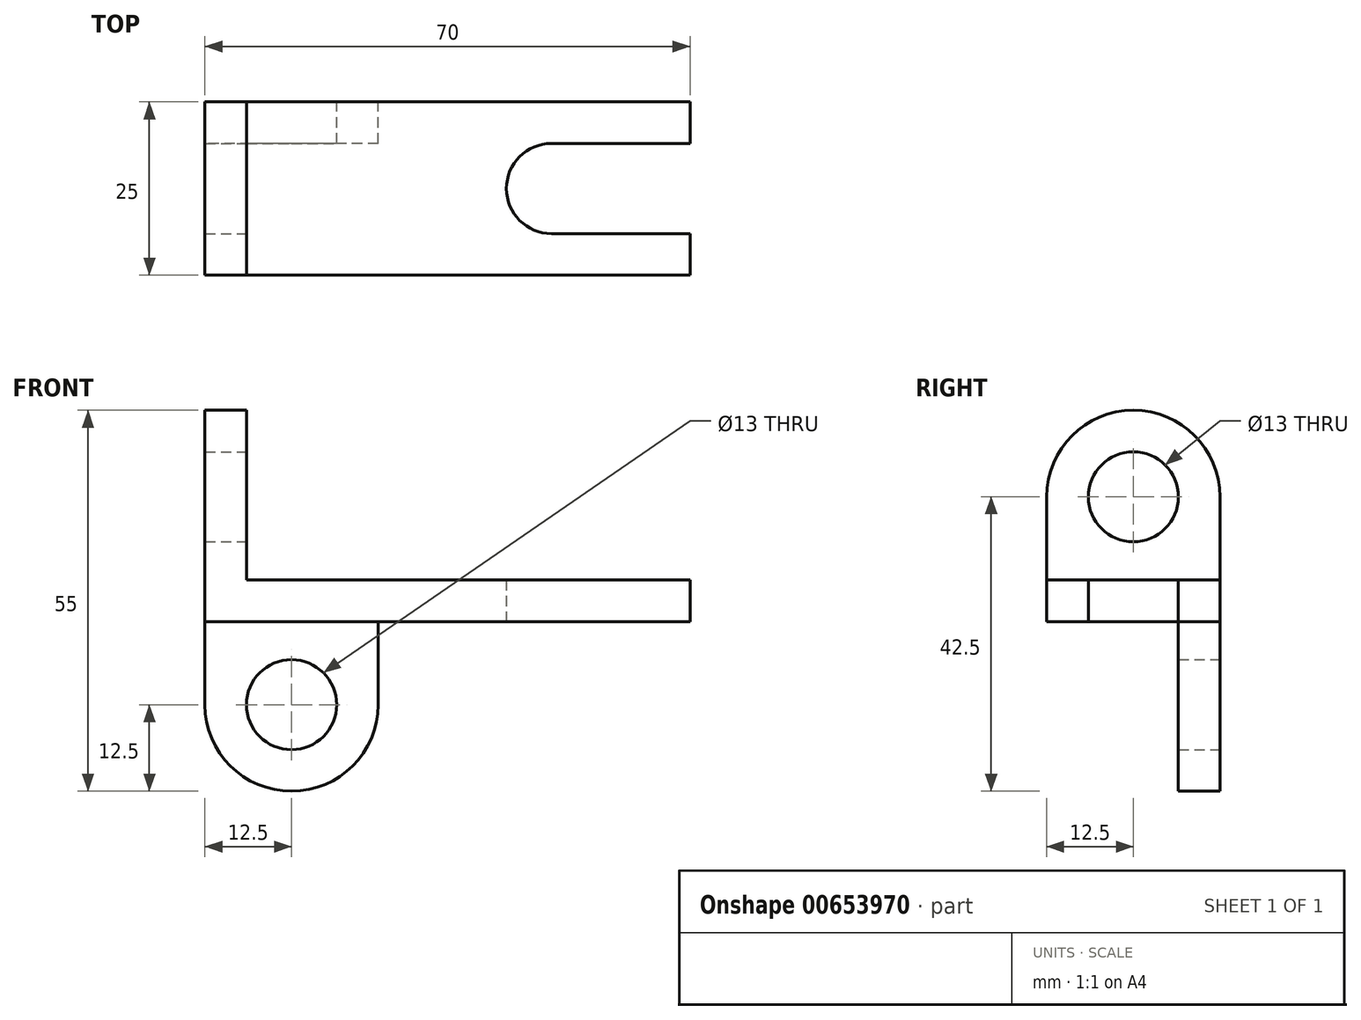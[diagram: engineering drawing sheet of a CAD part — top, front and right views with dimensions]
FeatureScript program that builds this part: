
annotation { "Feature Type Name" : "Feature", "Feature Type Description" : "" }
export const myFeature = defineFeature(function(context is Context, id is Id, definition is map)
    precondition{}
    {
        {
            var Q0;
            Q0=qCreatedBy(makeId("Top.planeOp"),FACE);
            var sketch = newSketch(context, id + "F0", { "sketchPlane" : qUnion([Q0])});
            skLineSegment(sketch, "E0.bottom", {"start": v(32, -12.5) * mm, "end": v(-32, -12.5) * mm});
            skLineSegment(sketch, "E0.top", {"start": v(32, 12.5) * mm, "end": v(-32, 12.5) * mm});
            skLineSegment(sketch, "E0.left", {"start": v(32, -12.5) * mm, "end": v(32, 12.5) * mm});
            skLineSegment(sketch, "E0.right", {"start": v(-32, -12.5) * mm, "end": v(-32, 12.5) * mm});
            skPoint(sketch, "E0.middle", {"position": v(0, 0) * mm});
            skLineSegment(sketch, "E1.bottom", {"start": v(32, 6.5) * mm, "end": v(12, 6.5) * mm});
            skLineSegment(sketch, "E1.top", {"start": v(32, -6.5) * mm, "end": v(12, -6.5) * mm});
            skLineSegment(sketch, "E1.left", {"start": v(32, 6.5) * mm, "end": v(32, -6.5) * mm});
            skLineSegment(sketch, "E1.right", {"start": v(12, 6.5) * mm, "end": v(12, -6.5) * mm});
            skPoint(sketch, "E1.middle", {"position": v(22, 0) * mm});
            skCircle(sketch, "E2", {"center": v(12, 0) * mm, "radius": 6.5 * mm});
            skSolve(sketch);
        }
        {
            var Q0;
            {var subQ4=sQuery(id+"F0.wireOp",EDGE,"E0.bottom");Q0=makeQuery(id+"F0.imprint","IMPRINT",FACE,{"disambiguationData":[TD([[makeQuery(id+"F0.imprint","IMPRINT",EDGE,{"derivedFrom":subQ4}),-1.0]])]});}
            extrude(context, id + "F1", {"entities" : qUnion([Q0]), "depth" : 6 * mm, "offsetDistance" : 25 * mm});
        }
        {
            var Q0;
            Q0=makeQuery(id+"F1.opExtrude","SWEPT_FACE",FACE,{"disambiguationData":[OSD([sQuery(id+"F0.wireOp",EDGE,"E0.right")])]});
            var sketch = newSketch(context, id + "F2", { "sketchPlane" : qUnion([Q0])});
            skLineSegment(sketch, "E3.bottom", {"start": v(-12.5, 0) * mm, "end": v(12.5, 0) * mm});
            skLineSegment(sketch, "E3.top", {"start": v(-12.5, 18) * mm, "end": v(-6.5, 18) * mm});
            skLineSegment(sketch, "E3.left", {"start": v(-12.5, 0) * mm, "end": v(-12.5, 18) * mm});
            skLineSegment(sketch, "E3.right", {"start": v(12.5, 0) * mm, "end": v(12.5, 18) * mm});
            skArc(sketch, "E4", {"start": v(12.5, 18) * mm, "mid": v(0, 30.5) * mm, "end": v(-12.5, 18) * mm});
            skCircle(sketch, "E5", {"center": v(0, 18) * mm, "radius": 6.5 * mm});
            skLineSegment(sketch, "E6.trimOffspring", {"start": v(6.5, 18) * mm, "end": v(12.5, 18) * mm});
            skSolve(sketch);
        }
        {
            var Q0;
            {var subQ1=sQuery(id+"F0.wireOp",EDGE,"E0.right");var subQ5=makeQuery(id+"F1.opExtrude","CAP_EDGE",EDGE,{"disambiguationData":[OSD([subQ1])],"isStart":false});Q0=makeQuery(id+"F2.imprint","IMPRINT",FACE,{"disambiguationData":[TD([[makeQuery(id+"F2.imprint","IMPRINT",EDGE,{"derivedFrom":subQ5}),1.0]])]});}
            var Q1;
            {var subQ3=sQuery(id+"F2.wireOp",EDGE,"E4");Q1=makeQuery(id+"F2.imprint","IMPRINT",FACE,{"disambiguationData":[TD([[makeQuery(id+"F2.imprint","IMPRINT",EDGE,{"derivedFrom":subQ3}),1.0]])]});}
            var Q2;
            {var subQ11=sQuery(id+"F2.wireOp",EDGE,"E3.right");Q2=makeQuery(id+"F2.imprint","IMPRINT",FACE,{"disambiguationData":[TD([[makeQuery(id+"F2.imprint","IMPRINT",EDGE,{"derivedFrom":subQ11}),1.0]])]});}
            extrude(context, id + "F3", {"entities" : qUnion([Q0, Q1, Q2]), "operationType" : NewBodyOperationType.ADD, "depth" : 6 * mm, "offsetDistance" : 25 * mm});
        }
        {
            var Q0;
            Q0=makeQuery(id+"F3.boolean.opBoolean","MERGE",FACE,{"derivedFrom":[makeQuery(id+"F1.opExtrude","SWEPT_FACE",FACE,{"disambiguationData":[OSD([sQuery(id+"F0.wireOp",EDGE,"E0.top")])]}),makeQuery(id+"F3.opExtrude","SWEPT_FACE",FACE,{"disambiguationData":[OSD([sQuery(id+"F2.wireOp",EDGE,"E3.left")])]})]});
            var sketch = newSketch(context, id + "F4", { "sketchPlane" : qUnion([Q0])});
            skLineSegment(sketch, "E7.bottom", {"start": v(38, 6) * mm, "end": v(13, 6) * mm});
            skLineSegment(sketch, "E7.top", {"start": v(38, -12) * mm, "end": v(13, -12) * mm});
            skLineSegment(sketch, "E7.left", {"start": v(38, 6) * mm, "end": v(38, -12) * mm});
            skLineSegment(sketch, "E7.right", {"start": v(13, 6) * mm, "end": v(13, -12) * mm});
            skCircle(sketch, "E8", {"center": v(25.5, -12) * mm, "radius": 12.5 * mm});
            skCircle(sketch, "E9", {"center": v(25.5, -12) * mm, "radius": 6.5 * mm});
            skSolve(sketch);
        }
        {
            var Q0;
            Q0 = qSketchRegion(id + "F4", true);
            extrude(context, id + "F5", {"entities" : qUnion([Q0]), "operationType" : NewBodyOperationType.ADD, "oppositeDirection" : true, "depth" : 6 * mm, "offsetDistance" : 25 * mm});
        }
    });
